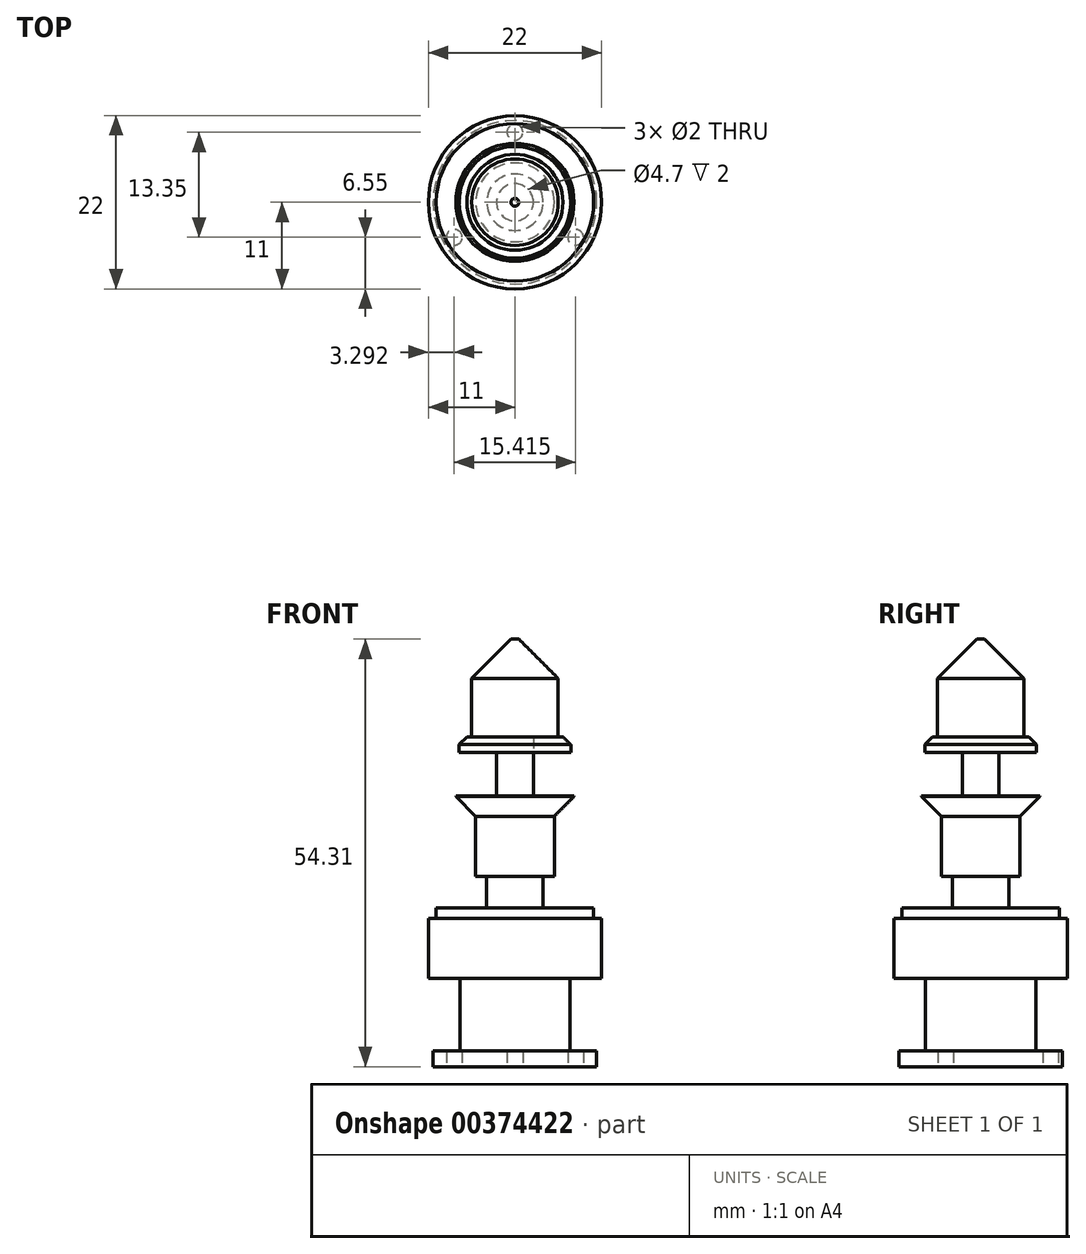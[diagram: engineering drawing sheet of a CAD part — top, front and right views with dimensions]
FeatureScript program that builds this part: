
annotation { "Feature Type Name" : "Feature", "Feature Type Description" : "" }
export const myFeature = defineFeature(function(context is Context, id is Id, definition is map)
    precondition{}
    {
        {
            var Q0;
            Q0=qCreatedBy(makeId("Top.planeOp"),FACE);
            var sketch = newSketch(context, id + "F0", { "sketchPlane" : qUnion([Q0])});
            skCircle(sketch, "E0", {"center": v(0, 0) * mm, "radius": 10.39 * mm});
            skCircle(sketch, "E1", {"center": v(0, 0) * mm, "radius": 8.9 * mm});
            skCircle(sketch, "E2", {"center": v(0, 8.9) * mm, "radius": 1 * mm});
            skCircle(sketch, "E3.1.0", {"center": v(-7.7, -4.45) * mm, "radius": 1 * mm});
            skCircle(sketch, "E3.2.0", {"center": v(7.7, -4.45) * mm, "radius": 1 * mm});
            skSolve(sketch);
        }
        {
            var Q0;
            Q0=qSketchRegion(id+"F0",true);
            var Q1;
            {var subQ0=sQuery(id+"F0.wireOp",EDGE,"E2");var subQ1=sQuery(id+"F0.wireOp",EDGE,"E1");var subQ2=makeQuery(id+"F0.imprint","INTERSECT",VERTEX,{"disambiguationData":[OD(0.0)],"derivedFrom":[subQ1,subQ0]});Q1=makeQuery(id+"F0.imprint","IMPRINT",FACE,{"disambiguationData":[TD([[makeQuery(id+"F0.imprint","IMPRINT",EDGE,{"disambiguationData":[TD([[subQ2,-1.0]])],"derivedFrom":subQ1}),1.0]])]});}
            extrude(context, id + "F1", {"entities" : qUnion([Q0, Q1]), "depth" : 2 * mm});
        }
        {
            var Q0;
            Q0=makeQuery(id+"F1.opExtrude","CAP_FACE",FACE,{"disambiguationData":[OSD([sQuery(id+"F0.wireOp",EDGE,"E0")])],"isStart":false});
            var sketch = newSketch(context, id + "F2", { "sketchPlane" : qUnion([Q0])});
            skCircle(sketch, "E4", {"center": v(0, 0) * mm, "radius": 7 * mm});
            skSolve(sketch);
        }
        {
            var Q0;
            Q0=qSketchRegion(id+"F2",true);
            extrude(context, id + "F3", {"entities" : qUnion([Q0]), "operationType" : NewBodyOperationType.ADD, "depth" : 9.2 * mm});
        }
        {
            var Q0;
            Q0=makeQuery(id+"F3.opExtrude","CAP_FACE",FACE,{"disambiguationData":[OSD([sQuery(id+"F2.wireOp",EDGE,"E4")])],"isStart":false});
            var sketch = newSketch(context, id + "F4", { "sketchPlane" : qUnion([Q0])});
            skCircle(sketch, "E5", {"center": v(0, 0) * mm, "radius": 11 * mm});
            skSolve(sketch);
        }
        {
            var Q0;
            Q0=makeQuery(id+"F4.imprint","IMPRINT",FACE,{"disambiguationData":[TD([[makeQuery(id+"F4.imprint","IMPRINT",EDGE,{"derivedFrom":sQuery(id+"F4.wireOp",EDGE,"E5")}),1.0]])]});
            var Q1;
            Q1=makeQuery(id+"F4.imprint","IMPRINT",FACE,{"disambiguationData":[TD([[makeQuery(id+"F4.imprint","IMPRINT",EDGE,{"derivedFrom":makeQuery(id+"F3.opExtrude","CAP_EDGE",EDGE,{"disambiguationData":[OSD([sQuery(id+"F2.wireOp",EDGE,"E4")])],"isStart":false})}),1.0]])]});
            extrude(context, id + "F5", {"entities" : qUnion([Q0, Q1]), "operationType" : NewBodyOperationType.ADD, "depth" : 7.66 * mm});
        }
        {
            var Q0;
            Q0=makeQuery(id+"F5.opExtrude","CAP_FACE",FACE,{"disambiguationData":[OSD([sQuery(id+"F4.wireOp",EDGE,"E5")])],"isStart":false});
            var sketch = newSketch(context, id + "F6", { "sketchPlane" : qUnion([Q0])});
            skCircle(sketch, "E6", {"center": v(0, 0) * mm, "radius": 10 * mm});
            skSolve(sketch);
        }
        {
            var Q0;
            Q0=makeQuery(id+"F6.imprint","IMPRINT",FACE,{"disambiguationData":[TD([[makeQuery(id+"F6.imprint","IMPRINT",EDGE,{"derivedFrom":sQuery(id+"F6.wireOp",EDGE,"E6")}),1.0]])]});
            extrude(context, id + "F7", {"entities" : qUnion([Q0]), "operationType" : NewBodyOperationType.ADD, "depth" : 1.33 * mm});
        }
        {
            var Q0;
            Q0=makeQuery(id+"F7.opExtrude","CAP_FACE",FACE,{"disambiguationData":[OSD([sQuery(id+"F6.wireOp",EDGE,"E6")])],"isStart":false});
            var sketch = newSketch(context, id + "F8", { "sketchPlane" : qUnion([Q0])});
            skCircle(sketch, "E7", {"center": v(0, 0) * mm, "radius": 3.58 * mm});
            skSolve(sketch);
        }
        {
            var Q0;
            Q0=qSketchRegion(id+"F8",true);
            extrude(context, id + "F9", {"entities" : qUnion([Q0]), "operationType" : NewBodyOperationType.ADD, "depth" : 4 * mm});
        }
        {
            var Q0;
            Q0=makeQuery(id+"F9.opExtrude","CAP_FACE",FACE,{"disambiguationData":[OSD([sQuery(id+"F8.wireOp",EDGE,"E7")])],"isStart":false});
            var sketch = newSketch(context, id + "F10", { "sketchPlane" : qUnion([Q0])});
            skCircle(sketch, "E8", {"center": v(0, 0) * mm, "radius": 5 * mm});
            skSolve(sketch);
        }
        {
            var Q0;
            Q0=qSketchRegion(id+"F10",true);
            extrude(context, id + "F11", {"entities" : qUnion([Q0]), "operationType" : NewBodyOperationType.ADD, "depth" : 7.62 * mm});
        }
        {
            var Q0;
            Q0=makeQuery(id+"F11.opExtrude","CAP_FACE",FACE,{"disambiguationData":[OSD([sQuery(id+"F10.wireOp",EDGE,"E8")])],"isStart":false});
            var sketch = newSketch(context, id + "F12", { "sketchPlane" : qUnion([Q0])});
            skCircle(sketch, "E9", {"center": v(0, 0) * mm, "radius": 7.5 * mm});
            skSolve(sketch);
        }
        {
            var Q0;
            Q0=qSketchRegion(id+"F12",true);
            extrude(context, id + "F13", {"entities" : qUnion([Q0]), "operationType" : NewBodyOperationType.ADD, "depth" : 2.6 * mm});
        }
        {
            var Q0;
            Q0=makeQuery(id+"F13.opExtrude","CAP_EDGE",EDGE,{"disambiguationData":[OSD([sQuery(id+"F12.wireOp",EDGE,"E9")])],"isStart":true});
            chamfer(context, id + "F14", {"entities" : qUnion([Q0]), "width" : 2.5 * mm, "tangentPropagation" : true});
        }
        {
            var Q0;
            Q0=makeQuery(id+"F13.opExtrude","CAP_FACE",FACE,{"disambiguationData":[OSD([sQuery(id+"F12.wireOp",EDGE,"E9")])],"isStart":false});
            var sketch = newSketch(context, id + "F15", { "sketchPlane" : qUnion([Q0])});
            skCircle(sketch, "E10", {"center": v(0, 0) * mm, "radius": 2.35 * mm});
            skSolve(sketch);
        }
        {
            var Q0;
            Q0=qSketchRegion(id+"F15",true);
            extrude(context, id + "F16", {"entities" : qUnion([Q0]), "operationType" : NewBodyOperationType.ADD, "depth" : 5.5 * mm});
        }
        {
            var Q0;
            Q0=makeQuery(id+"F16.opExtrude","CAP_FACE",FACE,{"disambiguationData":[OSD([sQuery(id+"F15.wireOp",EDGE,"E10")])],"isStart":false});
            var sketch = newSketch(context, id + "F17", { "sketchPlane" : qUnion([Q0])});
            skCircle(sketch, "E11", {"center": v(0, 0) * mm, "radius": 7.1 * mm});
            skSolve(sketch);
        }
        {
            var Q0;
            Q0=makeQuery(id+"F17.imprint","IMPRINT",FACE,{"disambiguationData":[TD([[makeQuery(id+"F17.imprint","IMPRINT",EDGE,{"derivedFrom":sQuery(id+"F17.wireOp",EDGE,"E11")}),1.0]])]});
            extrude(context, id + "F18", {"entities" : qUnion([Q0]), "depth" : 2 * mm});
        }
        {
            var Q0;
            Q0=makeQuery(id+"F18.opExtrude","CAP_EDGE",EDGE,{"disambiguationData":[OSD([sQuery(id+"F17.wireOp",EDGE,"E11")])],"isStart":false});
            chamfer(context, id + "F19", {"entities" : qUnion([Q0]), "width" : 1 * mm, "tangentPropagation" : true});
        }
        {
            var Q0;
            Q0=makeQuery(id+"F18.opExtrude","CAP_FACE",FACE,{"disambiguationData":[OSD([sQuery(id+"F15.wireOp",EDGE,"E10"),sQuery(id+"F17.wireOp",EDGE,"E11")])],"isStart":false});
            var sketch = newSketch(context, id + "F20", { "sketchPlane" : qUnion([Q0])});
            skCircle(sketch, "E12", {"center": v(0, 0) * mm, "radius": 5.5 * mm});
            skSolve(sketch);
        }
        {
            var Q0;
            Q0=qSketchRegion(id+"F20",true);
            extrude(context, id + "F21", {"entities" : qUnion([Q0]), "operationType" : NewBodyOperationType.ADD, "depth" : 12.4 * mm});
        }
        {
            var Q0;
            Q0=makeQuery(id+"F21.opExtrude","CAP_FACE",FACE,{"disambiguationData":[OSD([sQuery(id+"F20.wireOp",EDGE,"E12")])],"isStart":false});
            chamfer(context, id + "F22", {"entities" : qUnion([Q0]), "width" : 5 * mm, "tangentPropagation" : true});
        }
    });
